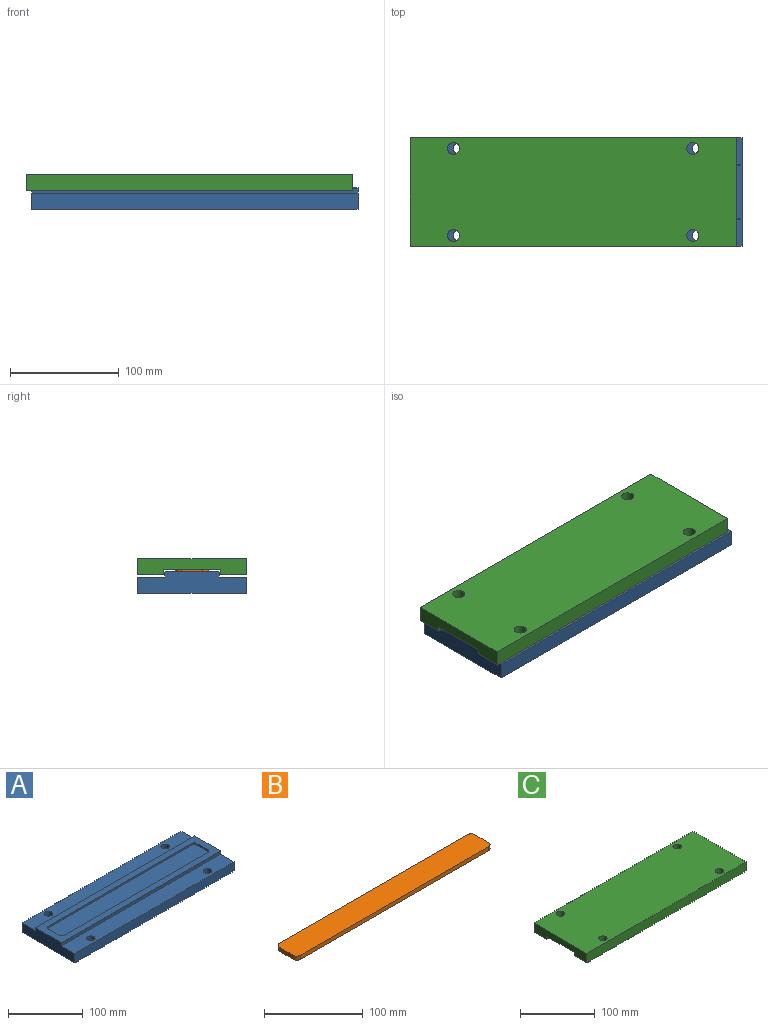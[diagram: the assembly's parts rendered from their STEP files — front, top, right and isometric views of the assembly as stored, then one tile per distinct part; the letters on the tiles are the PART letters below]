
ASSEMBLY  parts=3 mates=5
PART A: 25 faces, bbox 300x100x20 mm
  f0: plane 100x20mm, normal (-1,0,0), area 1749.7mm2, adj f1,f3,f4,f5,f6,f7,f8,f9
  f1: plane 300x15mm, normal (0,-1,0), area 4500mm2, adj f0,f2,f5,f7
  f2: plane 100x20mm, normal (1,0,0), area 1749.7mm2, adj f1,f3,f4,f5,f6,f7,f8,f9
  f3: plane 300x15mm, normal (0,1,0), area 4500mm2, adj f0,f2,f5,f9
  f4: plane 300x49mm, normal (0,0,1), area 6321.5mm2, adj f0,f2,f10,f11,f12,f13,f14,f15
  f5: plane 300x100mm, normal (0,0,-1), area 29619.9mm2, adj f0,f1,f2,f3,f21,f22,f23,f24
  f6: plane 300x4.5mm, normal (0,-1,0), area 1350mm2, adj f0,f2,f7,f11
  f7: plane 300x25mm, normal (0,0,1), area 7309.9mm2, adj f0,f1,f2,f6,f23,f24
  f8: plane 300x4.5mm, normal (0,1,0), area 1350mm2, adj f0,f2,f9,f10
  f9: plane 300x25mm, normal (0,0,1), area 7309.9mm2, adj f0,f2,f3,f8,f21,f22
  f10: plane 300x0.5mm, normal (0,0.71,0.71), area 212.1mm2, adj f0,f2,f4,f8
  f11: plane 300x0.5mm, normal (0,-0.71,0.71), area 212.1mm2, adj f0,f2,f4,f6
  f12: plane 20x3mm, normal (1,0,0), area 60mm2, adj f4,f13,f19,f20
  f13: cylinder r=5mm len=5mm, axis (0,0,1), area 23.6mm2, adj f4,f12,f14,f20
  f14: plane 270x3mm, normal (0,1,0), area 810mm2, adj f4,f13,f15,f20
  f15: cylinder r=5mm len=5mm, axis (0,0,1), area 23.6mm2, adj f4,f14,f16,f20
  f16: plane 20x3mm, normal (-1,0,0), area 60mm2, adj f4,f15,f17,f20
  f17: cylinder r=5mm len=5mm, axis (0,0,1), area 23.6mm2, adj f4,f16,f18,f20
  f18: plane 270x3mm, normal (0,-1,0), area 810mm2, adj f4,f17,f19,f20
  f19: cylinder r=5mm len=5mm, axis (0,0,1), area 23.6mm2, adj f4,f12,f18,f20
  f20: plane 280x30mm, normal (0,0,1), area 8378.5mm2, adj f12,f13,f14,f15,f16,f17,f18,f19
  f21: cylinder r=5.5mm len=15mm, axis (0,0,-1), area 518.4mm2, adj f5,f9
  f22: cylinder r=5.5mm len=15mm, axis (0,0,-1), area 518.4mm2, adj f5,f9
  f23: cylinder r=5.5mm len=15mm, axis (0,0,-1), area 518.4mm2, adj f5,f7
  f24: cylinder r=5.5mm len=15mm, axis (0,0,-1), area 518.4mm2, adj f5,f7
PART B: 10 faces, bbox 280x30x5 mm
  f0: plane 20x5mm, normal (-1,0,0), area 100mm2, adj f1,f7,f8,f9
  f1: cylinder r=5mm len=5mm, axis (0,0,-1), area 39.3mm2, adj f0,f2,f8,f9
  f2: plane 270x5mm, normal (0,-1,0), area 1350mm2, adj f1,f3,f8,f9
  f3: cylinder r=5mm len=5mm, axis (0,0,-1), area 39.3mm2, adj f2,f4,f8,f9
  f4: plane 20x5mm, normal (1,0,0), area 100mm2, adj f3,f5,f8,f9
  f5: cylinder r=5mm len=5mm, axis (0,0,-1), area 39.3mm2, adj f4,f6,f8,f9
  f6: plane 270x5mm, normal (0,1,0), area 1350mm2, adj f5,f7,f8,f9
  f7: cylinder r=5mm len=5mm, axis (0,0,-1), area 39.3mm2, adj f0,f6,f8,f9
  f8: plane 280x30mm, normal (0,0,1), area 8378.5mm2, adj f0,f1,f2,f3,f4,f5,f6,f7
  f9: plane 280x30mm, normal (0,0,-1), area 8378.5mm2, adj f0,f1,f2,f3,f4,f5,f6,f7
PART C: 16 faces, bbox 300x100x15 mm
  f0: plane 300x23.5mm, normal (0,0,-1), area 6859.9mm2, adj f1,f3,f4,f10,f14,f15
  f1: plane 100x15mm, normal (-1,0,0), area 1239.7mm2, adj f0,f2,f4,f5,f6,f7,f8,f9
  f2: plane 300x15mm, normal (0,-1,0), area 4500mm2, adj f1,f3,f5,f6
  f3: plane 100x15mm, normal (1,0,0), area 1239.8mm2, adj f0,f2,f4,f5,f6,f7,f8,f9
  f4: plane 300x15mm, normal (0,1,0), area 4500mm2, adj f0,f1,f3,f5
  f5: plane 300x100mm, normal (0,0,1), area 29619.9mm2, adj f1,f2,f3,f4,f12,f13,f14,f15
  f6: plane 300x23.5mm, normal (0,0,-1), area 6859.9mm2, adj f1,f2,f3,f11,f12,f13
  f7: plane 300x4.5mm, normal (0,1,0), area 1350mm2, adj f1,f3,f9,f11
  f8: plane 300x4.5mm, normal (0,-1,0), area 1350mm2, adj f1,f3,f9,f10
  f9: plane 300x52mm, normal (0,0,-1), area 15600mm2, adj f1,f3,f7,f8
  f10: plane 300x0.5mm, normal (0,-0.71,-0.71), area 212.1mm2, adj f0,f1,f3,f8
  f11: plane 300x0.5mm, normal (0,0.71,-0.71), area 212.1mm2, adj f1,f3,f6,f7
  f12: cylinder r=5.5mm len=15mm, axis (0,0,1), area 518.4mm2, adj f5,f6
  f13: cylinder r=5.5mm len=15mm, axis (0,0,1), area 518.4mm2, adj f5,f6
  f14: cylinder r=5.5mm len=15mm, axis (0,0,1), area 518.4mm2, adj f0,f5
  f15: cylinder r=5.5mm len=15mm, axis (0,0,1), area 518.4mm2, adj f0,f5
PLACE A t=(-10.06,29.61,-11.78)mm fixed
PLACE B t=(-0.06,64.61,5.22)mm
PLACE C t=(-15.24,29.61,5.22)mm
MATE planar C.f2 <-> A.f1  axis (0,-1,0) through (134.76,29.61,12.72)mm
MATE planar B.f9 <-> A.f20  axis (0,0,-1) through (139.94,79.61,5.22)mm
MATE planar B.f6 <-> A.f18  axis (0,1,0) through (139.94,94.61,7.72)mm
MATE planar C.f9 <-> B.f8  axis (0,0,-1) through (134.76,79.61,10.22)mm
MATE planar B.f0 <-> A.f12  axis (-1,0,0) through (-0.06,79.61,7.72)mm
